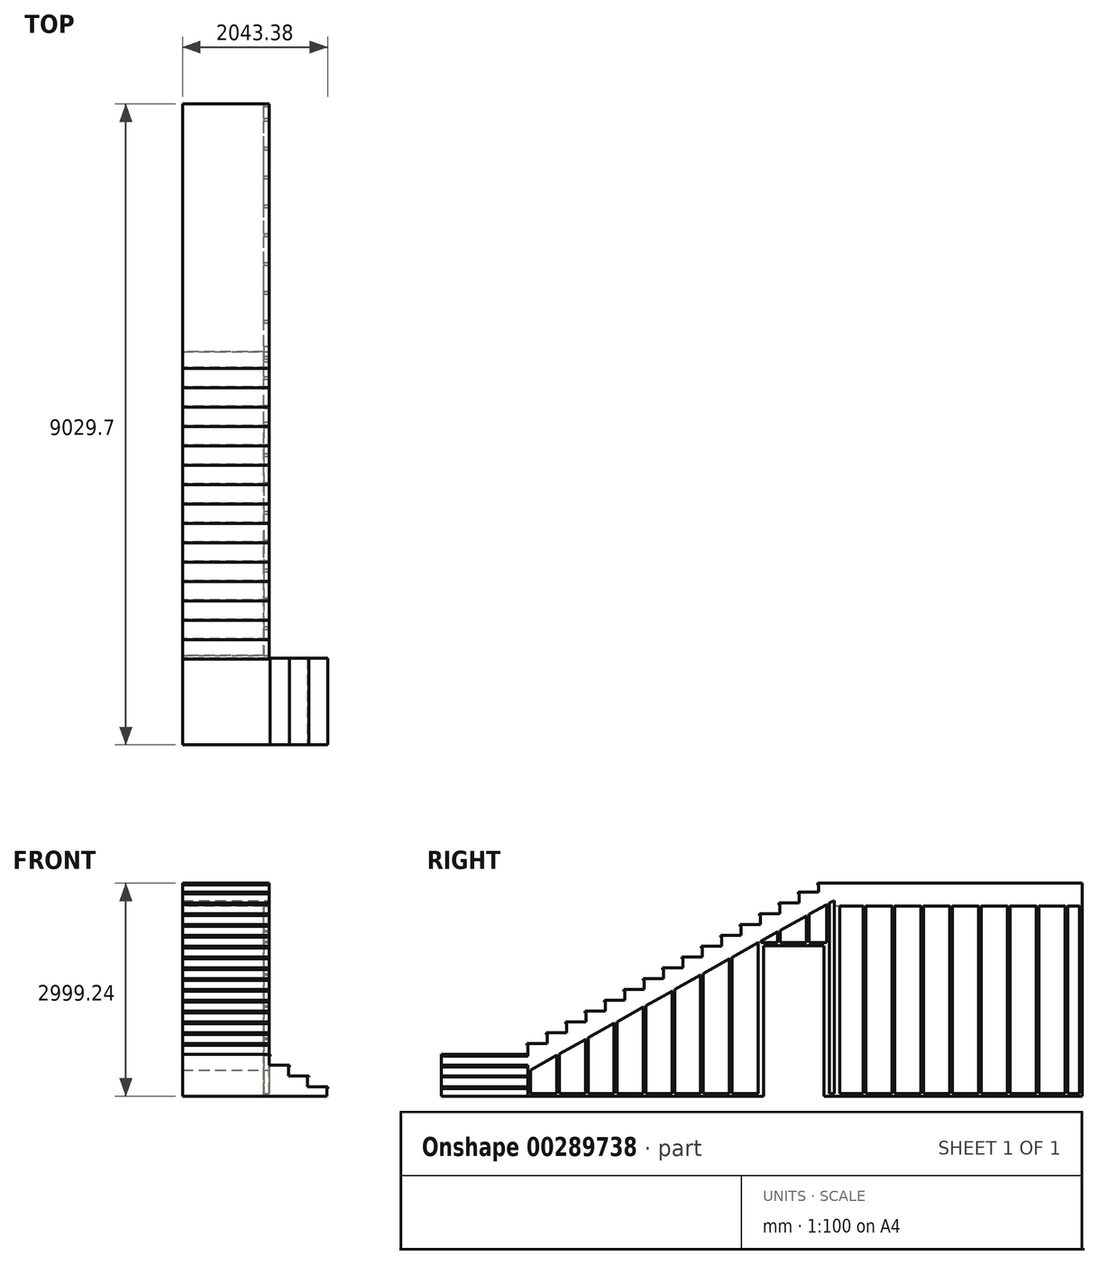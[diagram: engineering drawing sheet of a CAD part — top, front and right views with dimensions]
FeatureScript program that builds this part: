
annotation { "Feature Type Name" : "Feature", "Feature Type Description" : "" }
export const myFeature = defineFeature(function(context is Context, id is Id, definition is map)
    precondition{}
    {
        {
            var Q0;
            Q0=qCreatedBy(makeId("Right.planeOp"),FACE);
            var sketch = newSketch(context, id + "F0", { "sketchPlane" : qUnion([Q0])});
            skLineSegment(sketch, "E0.top", {"start": v(4540.25, 1499.62) * mm, "end": v(-4540.25, 1499.62) * mm});
            skLineSegment(sketch, "E0.left", {"start": v(4540.25, -1499.62) * mm, "end": v(4540.25, 1499.62) * mm});
            skLineSegment(sketch, "E0.right", {"start": v(-4540.25, -1499.62) * mm, "end": v(-4540.25, 1499.62) * mm});
            skPoint(sketch, "E0.middle", {"position": v(0, 0) * mm});
            skLineSegment(sketch, "E1", {"start": v(813.4, 1499.62) * mm, "end": v(813.4, 1478.97) * mm});
            skLineSegment(sketch, "E2", {"start": v(813.4, 1478.97) * mm, "end": v(826.1, 1478.97) * mm});
            skLineSegment(sketch, "E3", {"start": v(826.1, 1478.97) * mm, "end": v(826.1, 1371.6) * mm});
            skLineSegment(sketch, "E4", {"start": v(826.1, 1371.6) * mm, "end": v(540.36, 1371.6) * mm});
            skLineSegment(sketch, "E5", {"start": v(540.36, 1371.6) * mm, "end": v(540.36, 1350.87) * mm});
            skLineSegment(sketch, "E6", {"start": v(540.36, 1350.87) * mm, "end": v(553.16, 1350.87) * mm});
            skLineSegment(sketch, "E7", {"start": v(553.16, 1350.87) * mm, "end": v(553.16, 1219.2) * mm});
            skLineSegment(sketch, "E8", {"start": v(553.16, 1219.2) * mm, "end": v(267.26, 1219.2) * mm});
            skLineSegment(sketch, "E9", {"start": v(267.26, 1219.2) * mm, "end": v(267.26, 1198.47) * mm});
            skLineSegment(sketch, "E10", {"start": v(267.26, 1198.47) * mm, "end": v(280.06, 1198.47) * mm});
            skLineSegment(sketch, "E11", {"start": v(280.06, 1198.47) * mm, "end": v(280.06, 1066.8) * mm});
            skLineSegment(sketch, "E12", {"start": v(280.06, 1066.8) * mm, "end": v(-5.85, 1066.8) * mm});
            skLineSegment(sketch, "E13", {"start": v(-5.85, 1066.8) * mm, "end": v(-5.85, 1046.07) * mm});
            skLineSegment(sketch, "E14", {"start": v(-5.85, 1046.07) * mm, "end": v(6.96, 1046.07) * mm});
            skLineSegment(sketch, "E15", {"start": v(6.96, 1046.07) * mm, "end": v(6.96, 914.4) * mm});
            skLineSegment(sketch, "E16", {"start": v(6.96, 914.4) * mm, "end": v(-278.95, 914.4) * mm});
            skLineSegment(sketch, "E17", {"start": v(-278.95, 914.4) * mm, "end": v(-278.95, 893.67) * mm});
            skLineSegment(sketch, "E18", {"start": v(-278.95, 893.67) * mm, "end": v(-266.14, 893.67) * mm});
            skLineSegment(sketch, "E19", {"start": v(-266.14, 893.67) * mm, "end": v(-266.14, 762) * mm});
            skLineSegment(sketch, "E20", {"start": v(-266.14, 762) * mm, "end": v(-552.05, 762) * mm});
            skLineSegment(sketch, "E21", {"start": v(-552.05, 762) * mm, "end": v(-552.05, 741.27) * mm});
            skLineSegment(sketch, "E22", {"start": v(-552.05, 741.27) * mm, "end": v(-539.25, 741.27) * mm});
            skLineSegment(sketch, "E23", {"start": v(-539.25, 741.27) * mm, "end": v(-539.25, 609.6) * mm});
            skLineSegment(sketch, "E24", {"start": v(-539.25, 609.6) * mm, "end": v(-825.15, 609.6) * mm});
            skLineSegment(sketch, "E25", {"start": v(-825.15, 609.6) * mm, "end": v(-825.15, 588.87) * mm});
            skLineSegment(sketch, "E26", {"start": v(-825.15, 588.87) * mm, "end": v(-812.35, 588.87) * mm});
            skLineSegment(sketch, "E27", {"start": v(-812.35, 588.87) * mm, "end": v(-812.35, 457.2) * mm});
            skLineSegment(sketch, "E28", {"start": v(-812.35, 457.2) * mm, "end": v(-1098.25, 457.2) * mm});
            skLineSegment(sketch, "E29", {"start": v(-1098.25, 457.2) * mm, "end": v(-1098.25, 436.47) * mm});
            skLineSegment(sketch, "E30", {"start": v(-1098.25, 436.47) * mm, "end": v(-1085.45, 436.47) * mm});
            skLineSegment(sketch, "E31", {"start": v(-1085.45, 436.47) * mm, "end": v(-1085.45, 304.8) * mm});
            skLineSegment(sketch, "E32", {"start": v(-1085.45, 304.8) * mm, "end": v(-1371.35, 304.8) * mm});
            skLineSegment(sketch, "E33", {"start": v(-1371.35, 304.8) * mm, "end": v(-1371.35, 284.07) * mm});
            skLineSegment(sketch, "E34", {"start": v(-1371.35, 284.07) * mm, "end": v(-1358.55, 284.07) * mm});
            skLineSegment(sketch, "E35", {"start": v(-1358.55, 284.07) * mm, "end": v(-1358.55, 152.4) * mm});
            skLineSegment(sketch, "E36", {"start": v(-1358.55, 152.4) * mm, "end": v(-1644.45, 152.4) * mm});
            skLineSegment(sketch, "E37", {"start": v(-1644.45, 152.4) * mm, "end": v(-1644.45, 131.67) * mm});
            skLineSegment(sketch, "E38", {"start": v(-1644.45, 131.67) * mm, "end": v(-1631.65, 131.67) * mm});
            skLineSegment(sketch, "E39", {"start": v(-1631.65, 131.67) * mm, "end": v(-1631.65, 0) * mm});
            skLineSegment(sketch, "E40", {"start": v(-1631.65, 0) * mm, "end": v(-1917.55, 0) * mm});
            skLineSegment(sketch, "E41", {"start": v(-1917.55, 0) * mm, "end": v(-1917.55, -20.73) * mm});
            skLineSegment(sketch, "E42", {"start": v(-1917.55, -20.73) * mm, "end": v(-1904.75, -20.73) * mm});
            skLineSegment(sketch, "E43", {"start": v(-1904.75, -20.73) * mm, "end": v(-1904.75, -152.4) * mm});
            skLineSegment(sketch, "E44", {"start": v(-1904.75, -152.4) * mm, "end": v(-2190.65, -152.4) * mm});
            skLineSegment(sketch, "E45", {"start": v(-2190.65, -152.4) * mm, "end": v(-2190.65, -173.13) * mm});
            skLineSegment(sketch, "E46", {"start": v(-2190.65, -173.13) * mm, "end": v(-2177.85, -173.13) * mm});
            skLineSegment(sketch, "E47", {"start": v(-2177.85, -173.13) * mm, "end": v(-2177.85, -304.8) * mm});
            skLineSegment(sketch, "E48", {"start": v(-2177.85, -304.8) * mm, "end": v(-2463.75, -304.8) * mm});
            skLineSegment(sketch, "E49", {"start": v(-2463.75, -304.8) * mm, "end": v(-2463.75, -325.53) * mm});
            skLineSegment(sketch, "E50", {"start": v(-2463.75, -325.53) * mm, "end": v(-2450.95, -325.53) * mm});
            skLineSegment(sketch, "E51", {"start": v(-2450.95, -325.53) * mm, "end": v(-2450.95, -457.2) * mm});
            skLineSegment(sketch, "E52", {"start": v(-2450.95, -457.2) * mm, "end": v(-2736.85, -457.2) * mm});
            skLineSegment(sketch, "E53", {"start": v(-2736.85, -457.2) * mm, "end": v(-2736.85, -477.93) * mm});
            skLineSegment(sketch, "E54", {"start": v(-2736.85, -477.93) * mm, "end": v(-2724.05, -477.93) * mm});
            skLineSegment(sketch, "E55", {"start": v(-2724.05, -477.93) * mm, "end": v(-2724.05, -609.6) * mm});
            skLineSegment(sketch, "E56", {"start": v(-2724.05, -609.6) * mm, "end": v(-3009.95, -609.6) * mm});
            skLineSegment(sketch, "E57", {"start": v(-3009.95, -609.6) * mm, "end": v(-3009.95, -630.33) * mm});
            skLineSegment(sketch, "E58", {"start": v(-3009.95, -630.33) * mm, "end": v(-2997.15, -630.33) * mm});
            skLineSegment(sketch, "E59", {"start": v(-2997.15, -630.33) * mm, "end": v(-2997.15, -762) * mm});
            skLineSegment(sketch, "E60", {"start": v(-2997.15, -762) * mm, "end": v(-3283.05, -762) * mm});
            skLineSegment(sketch, "E61", {"start": v(-3283.05, -762) * mm, "end": v(-3283.05, -782.73) * mm});
            skLineSegment(sketch, "E62", {"start": v(-3283.05, -782.73) * mm, "end": v(-3270.25, -782.73) * mm});
            skLineSegment(sketch, "E63", {"start": v(-3270.25, -782.73) * mm, "end": v(-3270.25, -914.4) * mm});
            skLineSegment(sketch, "E64", {"start": v(-3270.25, -914.4) * mm, "end": v(-4489.45, -914.4) * mm});
            skLineSegment(sketch, "E65", {"start": v(-4489.45, -914.4) * mm, "end": v(-4489.45, -1499.62) * mm});
            skLineSegment(sketch, "E66", {"start": v(-4540.25, -1499.62) * mm, "end": v(4540.25, -1499.62) * mm});
            skSolve(sketch);
        }
        {
            var Q0;
            {var subQ3=sQuery(id+"F0.wireOp",EDGE,"E1");Q0=makeQuery(id+"F0.imprint","IMPRINT",FACE,{"disambiguationData":[TD([[makeQuery(id+"F0.imprint","IMPRINT",EDGE,{"derivedFrom":subQ3}),1.0]])]});}
            extrude(context, id + "F1", {"entities" : qUnion([Q0]), "depth" : 2438.4 * mm, "offsetDistance" : 30.48 * mm});
        }
        {
            var Q0;
            Q0=makeQuery(id+"F1.opExtrude","SWEPT_FACE",FACE,{"disambiguationData":[OSD([sQuery(id+"F0.wireOp",EDGE,"E66")])]});
            var sketch = newSketch(context, id + "F2", { "sketchPlane" : qUnion([Q0])});
            skLineSegment(sketch, "E67", {"start": v(1219.2, -4540.25) * mm, "end": v(1219.2, 3270.25) * mm});
            skLineSegment(sketch, "E68", {"start": v(1219.2, 3270.25) * mm, "end": v(2438.4, 3270.25) * mm});
            skSolve(sketch);
        }
        {
            var Q0;
            {var subQ0=sQuery(id+"F2.wireOp",EDGE,"E67");Q0=makeQuery(id+"F2.imprint","IMPRINT",FACE,{"disambiguationData":[TD([[makeQuery(id+"F2.imprint","IMPRINT",EDGE,{"derivedFrom":subQ0}),-1.0]])]});}
            extrude(context, id + "F3", {"entities" : qUnion([Q0]), "operationType" : NewBodyOperationType.REMOVE, "oppositeDirection" : true, "depth" : 6096 * mm, "offsetDistance" : 30.48 * mm});
        }
        {
            var Q0;
            {var subQ0=sQuery(id+"F0.wireOp",EDGE,"E60");var subQ1=sQuery(id+"F0.wireOp",EDGE,"E61");var subQ2=sQuery(id+"F0.wireOp",EDGE,"E62");Q0=makeQuery(id+"F3.boolean.opBoolean","SPLIT",FACE,{"disambiguationData":[TD([makeQuery(id+"F1.opExtrude","SWEPT_FACE",FACE,{"disambiguationData":[OSD([subQ0])]})])],"derivedFrom":makeQuery(id+"F1.opExtrude","CAP_FACE",FACE,{"disambiguationData":[OSD([sQuery(id+"F0.wireOp",EDGE,"E0.top"),sQuery(id+"F0.wireOp",EDGE,"E0.left"),sQuery(id+"F0.wireOp",EDGE,"E1"),sQuery(id+"F0.wireOp",EDGE,"E2"),sQuery(id+"F0.wireOp",EDGE,"E3"),sQuery(id+"F0.wireOp",EDGE,"E4"),sQuery(id+"F0.wireOp",EDGE,"E5"),sQuery(id+"F0.wireOp",EDGE,"E6"),sQuery(id+"F0.wireOp",EDGE,"E7"),sQuery(id+"F0.wireOp",EDGE,"E8"),sQuery(id+"F0.wireOp",EDGE,"E9"),sQuery(id+"F0.wireOp",EDGE,"E10"),sQuery(id+"F0.wireOp",EDGE,"E11"),sQuery(id+"F0.wireOp",EDGE,"E12"),sQuery(id+"F0.wireOp",EDGE,"E13"),sQuery(id+"F0.wireOp",EDGE,"E14"),sQuery(id+"F0.wireOp",EDGE,"E15"),sQuery(id+"F0.wireOp",EDGE,"E16"),sQuery(id+"F0.wireOp",EDGE,"E17"),sQuery(id+"F0.wireOp",EDGE,"E18"),sQuery(id+"F0.wireOp",EDGE,"E19"),sQuery(id+"F0.wireOp",EDGE,"E20"),sQuery(id+"F0.wireOp",EDGE,"E21"),sQuery(id+"F0.wireOp",EDGE,"E22"),sQuery(id+"F0.wireOp",EDGE,"E23"),sQuery(id+"F0.wireOp",EDGE,"E24"),sQuery(id+"F0.wireOp",EDGE,"E25"),sQuery(id+"F0.wireOp",EDGE,"E26"),sQuery(id+"F0.wireOp",EDGE,"E27"),sQuery(id+"F0.wireOp",EDGE,"E28"),sQuery(id+"F0.wireOp",EDGE,"E29"),sQuery(id+"F0.wireOp",EDGE,"E30"),sQuery(id+"F0.wireOp",EDGE,"E31"),sQuery(id+"F0.wireOp",EDGE,"E32"),sQuery(id+"F0.wireOp",EDGE,"E33"),sQuery(id+"F0.wireOp",EDGE,"E34"),sQuery(id+"F0.wireOp",EDGE,"E35"),sQuery(id+"F0.wireOp",EDGE,"E36"),sQuery(id+"F0.wireOp",EDGE,"E37"),sQuery(id+"F0.wireOp",EDGE,"E38"),sQuery(id+"F0.wireOp",EDGE,"E39"),sQuery(id+"F0.wireOp",EDGE,"E40"),sQuery(id+"F0.wireOp",EDGE,"E41"),sQuery(id+"F0.wireOp",EDGE,"E42"),sQuery(id+"F0.wireOp",EDGE,"E43"),sQuery(id+"F0.wireOp",EDGE,"E44"),sQuery(id+"F0.wireOp",EDGE,"E45"),sQuery(id+"F0.wireOp",EDGE,"E46"),sQuery(id+"F0.wireOp",EDGE,"E47"),sQuery(id+"F0.wireOp",EDGE,"E48"),sQuery(id+"F0.wireOp",EDGE,"E49"),sQuery(id+"F0.wireOp",EDGE,"E50"),sQuery(id+"F0.wireOp",EDGE,"E51"),sQuery(id+"F0.wireOp",EDGE,"E52"),sQuery(id+"F0.wireOp",EDGE,"E53"),sQuery(id+"F0.wireOp",EDGE,"E54"),sQuery(id+"F0.wireOp",EDGE,"E55"),sQuery(id+"F0.wireOp",EDGE,"E56"),sQuery(id+"F0.wireOp",EDGE,"E57"),sQuery(id+"F0.wireOp",EDGE,"E58"),sQuery(id+"F0.wireOp",EDGE,"E59"),subQ0,subQ1,subQ2,sQuery(id+"F0.wireOp",EDGE,"E63"),sQuery(id+"F0.wireOp",EDGE,"E64"),sQuery(id+"F0.wireOp",EDGE,"E65"),sQuery(id+"F0.wireOp",EDGE,"E66")])],"isStart":false})});}
            extrude(context, id + "F4", {"entities" : qUnion([Q0]), "operationType" : NewBodyOperationType.REMOVE, "oppositeDirection" : true, "depth" : 1219.2 * mm, "offsetDistance" : 30.48 * mm});
        }
        {
            var Q0;
            Q0=makeQuery(id+"F1.opExtrude","SWEPT_FACE",FACE,{"disambiguationData":[OSD([sQuery(id+"F0.wireOp",EDGE,"E65")])]});
            var sketch = newSketch(context, id + "F5", { "sketchPlane" : qUnion([Q0])});
            skLineSegment(sketch, "E69", {"start": v(1232, -914.4) * mm, "end": v(1232, -935.13) * mm});
            skLineSegment(sketch, "E70", {"start": v(1232, -935.13) * mm, "end": v(1219.2, -935.13) * mm});
            skLineSegment(sketch, "E71", {"start": v(1219.2, -935.13) * mm, "end": v(1219.2, -1066.8) * mm});
            skLineSegment(sketch, "E72", {"start": v(1219.2, -1066.8) * mm, "end": v(1505.1, -1066.8) * mm});
            skLineSegment(sketch, "E73", {"start": v(1505.1, -1066.8) * mm, "end": v(1505.1, -1087.53) * mm});
            skLineSegment(sketch, "E74", {"start": v(1505.1, -1087.53) * mm, "end": v(1492.3, -1087.53) * mm});
            skLineSegment(sketch, "E75", {"start": v(1492.3, -1087.53) * mm, "end": v(1492.3, -1219.2) * mm});
            skLineSegment(sketch, "E76", {"start": v(1492.3, -1219.2) * mm, "end": v(1778.2, -1219.2) * mm});
            skLineSegment(sketch, "E77", {"start": v(1778.2, -1219.2) * mm, "end": v(1778.2, -1232) * mm});
            skLineSegment(sketch, "E78", {"start": v(1778.2, -1232) * mm, "end": v(1757.48, -1232) * mm});
            skLineSegment(sketch, "E79", {"start": v(1757.48, -1232) * mm, "end": v(1757.48, -1371.6) * mm});
            skLineSegment(sketch, "E80", {"start": v(1757.48, -1371.6) * mm, "end": v(2043.38, -1371.6) * mm});
            skLineSegment(sketch, "E81", {"start": v(2043.38, -1371.6) * mm, "end": v(2043.38, -1392.33) * mm});
            skLineSegment(sketch, "E82", {"start": v(2043.38, -1392.33) * mm, "end": v(2030.58, -1392.33) * mm});
            skLineSegment(sketch, "E83", {"start": v(2030.58, -1392.33) * mm, "end": v(2030.58, -1499.62) * mm});
            skSolve(sketch);
        }
        {
            var Q0;
            Q0 = qSketchRegion(id + "F5", true);
            var Q1;
            {var subQ0=sQuery(id+"F5.wireOp",EDGE,"E69");Q1=makeQuery(id+"F5.imprint","IMPRINT",FACE,{"disambiguationData":[TD([[makeQuery(id+"F5.imprint","IMPRINT",EDGE,{"derivedFrom":subQ0}),1.0]])]});}
            extrude(context, id + "F6", {"entities" : qUnion([Q0, Q1]), "operationType" : NewBodyOperationType.REMOVE, "oppositeDirection" : true, "depth" : 12192 * mm, "offsetDistance" : 30.48 * mm});
        }
        {
            var Q0;
            Q0=makeQuery(id+"F6.boolean.opBoolean","MERGE",FACE,{"derivedFrom":[makeQuery(id+"F4.boolean.opBoolean","MERGE",FACE,{"derivedFrom":[makeQuery(id+"F3.boolean.opBoolean","COPY",FACE,{"derivedFrom":makeQuery(id+"F3.opExtrude","SWEPT_FACE",FACE,{"disambiguationData":[OSD([sQuery(id+"F2.wireOp",EDGE,"E67")])]})})],"fromTools":[makeQuery(id+"F4.opExtrude","CAP_FACE",FACE,{"disambiguationData":[OSD([sQuery(id+"F0.wireOp",EDGE,"E0.top"),sQuery(id+"F0.wireOp",EDGE,"E0.left"),sQuery(id+"F0.wireOp",EDGE,"E1"),sQuery(id+"F0.wireOp",EDGE,"E2"),sQuery(id+"F0.wireOp",EDGE,"E3"),sQuery(id+"F0.wireOp",EDGE,"E4"),sQuery(id+"F0.wireOp",EDGE,"E5"),sQuery(id+"F0.wireOp",EDGE,"E6"),sQuery(id+"F0.wireOp",EDGE,"E7"),sQuery(id+"F0.wireOp",EDGE,"E8"),sQuery(id+"F0.wireOp",EDGE,"E9"),sQuery(id+"F0.wireOp",EDGE,"E10"),sQuery(id+"F0.wireOp",EDGE,"E11"),sQuery(id+"F0.wireOp",EDGE,"E12"),sQuery(id+"F0.wireOp",EDGE,"E13"),sQuery(id+"F0.wireOp",EDGE,"E14"),sQuery(id+"F0.wireOp",EDGE,"E15"),sQuery(id+"F0.wireOp",EDGE,"E16"),sQuery(id+"F0.wireOp",EDGE,"E17"),sQuery(id+"F0.wireOp",EDGE,"E18"),sQuery(id+"F0.wireOp",EDGE,"E19"),sQuery(id+"F0.wireOp",EDGE,"E20"),sQuery(id+"F0.wireOp",EDGE,"E21"),sQuery(id+"F0.wireOp",EDGE,"E22"),sQuery(id+"F0.wireOp",EDGE,"E23"),sQuery(id+"F0.wireOp",EDGE,"E24"),sQuery(id+"F0.wireOp",EDGE,"E25"),sQuery(id+"F0.wireOp",EDGE,"E26"),sQuery(id+"F0.wireOp",EDGE,"E27"),sQuery(id+"F0.wireOp",EDGE,"E28"),sQuery(id+"F0.wireOp",EDGE,"E29"),sQuery(id+"F0.wireOp",EDGE,"E30"),sQuery(id+"F0.wireOp",EDGE,"E31"),sQuery(id+"F0.wireOp",EDGE,"E32"),sQuery(id+"F0.wireOp",EDGE,"E33"),sQuery(id+"F0.wireOp",EDGE,"E34"),sQuery(id+"F0.wireOp",EDGE,"E35"),sQuery(id+"F0.wireOp",EDGE,"E36"),sQuery(id+"F0.wireOp",EDGE,"E37"),sQuery(id+"F0.wireOp",EDGE,"E38"),sQuery(id+"F0.wireOp",EDGE,"E39"),sQuery(id+"F0.wireOp",EDGE,"E40"),sQuery(id+"F0.wireOp",EDGE,"E41"),sQuery(id+"F0.wireOp",EDGE,"E42"),sQuery(id+"F0.wireOp",EDGE,"E43"),sQuery(id+"F0.wireOp",EDGE,"E44"),sQuery(id+"F0.wireOp",EDGE,"E45"),sQuery(id+"F0.wireOp",EDGE,"E46"),sQuery(id+"F0.wireOp",EDGE,"E47"),sQuery(id+"F0.wireOp",EDGE,"E48"),sQuery(id+"F0.wireOp",EDGE,"E49"),sQuery(id+"F0.wireOp",EDGE,"E50"),sQuery(id+"F0.wireOp",EDGE,"E51"),sQuery(id+"F0.wireOp",EDGE,"E52"),sQuery(id+"F0.wireOp",EDGE,"E53"),sQuery(id+"F0.wireOp",EDGE,"E54"),sQuery(id+"F0.wireOp",EDGE,"E55"),sQuery(id+"F0.wireOp",EDGE,"E56"),sQuery(id+"F0.wireOp",EDGE,"E57"),sQuery(id+"F0.wireOp",EDGE,"E58"),sQuery(id+"F0.wireOp",EDGE,"E59"),sQuery(id+"F0.wireOp",EDGE,"E60"),sQuery(id+"F0.wireOp",EDGE,"E61"),sQuery(id+"F0.wireOp",EDGE,"E62"),sQuery(id+"F0.wireOp",EDGE,"E63"),sQuery(id+"F0.wireOp",EDGE,"E64"),sQuery(id+"F0.wireOp",EDGE,"E65"),sQuery(id+"F0.wireOp",EDGE,"E66")])],"isStart":false})]})],"fromTools":[makeQuery(id+"F6.opExtrude","SWEPT_FACE",FACE,{"disambiguationData":[OSD([sQuery(id+"F5.wireOp",EDGE,"E71")])]})]});
            var sketch = newSketch(context, id + "F7", { "sketchPlane" : qUnion([Q0])});
            skLineSegment(sketch, "E84", {"start": v(1406.1, 1499.62) * mm, "end": v(-3270.25, -1109.96) * mm});
            skLineSegment(sketch, "E85", {"start": v(-2997.15, -762) * mm, "end": v(-2724.05, -609.6) * mm});
            skLineSegment(sketch, "E86", {"start": v(1049.26, 1300.49) * mm, "end": v(1049.26, 1499.62) * mm});
            skLineSegment(sketch, "E87.bottom", {"start": v(1087.36, 1213.87) * mm, "end": v(4502.15, 1213.87) * mm});
            skLineSegment(sketch, "E87.top", {"start": v(1087.36, -1461.52) * mm, "end": v(4502.15, -1461.52) * mm});
            skLineSegment(sketch, "E87.left", {"start": v(1087.36, 1213.87) * mm, "end": v(1087.36, -1461.52) * mm});
            skLineSegment(sketch, "E87.right", {"start": v(4502.15, 1213.87) * mm, "end": v(4502.15, -1461.52) * mm});
            skLineSegment(sketch, "E88", {"start": v(1049.26, 1300.49) * mm, "end": v(1049.26, -1461.52) * mm});
            skLineSegment(sketch, "E89", {"start": v(1049.26, -1461.52) * mm, "end": v(-3232.15, -1461.52) * mm});
            skLineSegment(sketch, "E90", {"start": v(-3232.15, -1461.52) * mm, "end": v(-3232.15, -1132.33) * mm});
            skLineSegment(sketch, "E91", {"start": v(-3232.15, -1132.33) * mm, "end": v(1049.26, 1256.85) * mm});
            skLineSegment(sketch, "E92", {"start": v(-2825.85, -905.6) * mm, "end": v(-2825.85, -1461.52) * mm});
            skLineSegment(sketch, "E93", {"start": v(-2863.95, -926.86) * mm, "end": v(-2863.95, -1461.52) * mm});
            skLineSegment(sketch, "E94", {"start": v(-2457.66, -700.13) * mm, "end": v(-2457.66, -1461.52) * mm});
            skLineSegment(sketch, "E95", {"start": v(-2419.56, -678.87) * mm, "end": v(-2419.56, -1461.52) * mm});
            skLineSegment(sketch, "E96", {"start": v(-2051.36, -473.4) * mm, "end": v(-2051.36, -1461.52) * mm});
            skLineSegment(sketch, "E97", {"start": v(-2013.26, -452.14) * mm, "end": v(-2013.26, -1461.52) * mm});
            skLineSegment(sketch, "E98", {"start": v(-1645.06, -246.67) * mm, "end": v(-1645.06, -1461.52) * mm});
            skLineSegment(sketch, "E99", {"start": v(-1606.96, -225.41) * mm, "end": v(-1606.96, -1461.52) * mm});
            skLineSegment(sketch, "E100", {"start": v(-1238.76, -19.94) * mm, "end": v(-1238.76, -1461.52) * mm});
            skLineSegment(sketch, "E101", {"start": v(-1200.66, -1461.52) * mm, "end": v(-1200.66, 1.32) * mm});
            skLineSegment(sketch, "E102", {"start": v(-832.46, 206.79) * mm, "end": v(-832.46, -1461.52) * mm});
            skLineSegment(sketch, "E103", {"start": v(-794.36, 228.05) * mm, "end": v(-794.36, -1461.52) * mm});
            skLineSegment(sketch, "E104", {"start": v(-426.16, 433.51) * mm, "end": v(-426.16, -1461.52) * mm});
            skLineSegment(sketch, "E105", {"start": v(-388.06, 454.78) * mm, "end": v(-388.06, -1461.52) * mm});
            skLineSegment(sketch, "E106", {"start": v(-19.87, 660.24) * mm, "end": v(-19.87, -1461.52) * mm});
            skLineSegment(sketch, "E107", {"start": v(18.23, 681.5) * mm, "end": v(18.23, -1461.52) * mm});
            skLineSegment(sketch, "E108", {"start": v(1087.36, 1175.77) * mm, "end": v(4502.15, 1175.77) * mm});
            skLineSegment(sketch, "E109.bottom", {"start": v(1455.56, 1175.77) * mm, "end": v(1493.66, 1175.77) * mm});
            skLineSegment(sketch, "E109.top", {"start": v(1455.56, -1461.52) * mm, "end": v(1493.66, -1461.52) * mm});
            skLineSegment(sketch, "E109.left", {"start": v(1455.56, 1175.77) * mm, "end": v(1455.56, -1461.52) * mm});
            skLineSegment(sketch, "E109.right", {"start": v(1493.66, 1175.77) * mm, "end": v(1493.66, -1461.52) * mm});
            skLineSegment(sketch, "E110.bottom", {"start": v(1861.86, 1175.77) * mm, "end": v(1899.96, 1175.77) * mm});
            skLineSegment(sketch, "E110.top", {"start": v(1861.86, -1461.52) * mm, "end": v(1899.96, -1461.52) * mm});
            skLineSegment(sketch, "E110.left", {"start": v(1861.86, 1175.77) * mm, "end": v(1861.86, -1461.52) * mm});
            skLineSegment(sketch, "E110.right", {"start": v(1899.96, 1175.77) * mm, "end": v(1899.96, -1461.52) * mm});
            skLineSegment(sketch, "E111.bottom", {"start": v(56.33, -1499.62) * mm, "end": v(907.23, -1499.62) * mm});
            skLineSegment(sketch, "E111.top", {"start": v(56.33, 621.28) * mm, "end": v(907.23, 621.28) * mm});
            skLineSegment(sketch, "E111.left", {"start": v(56.33, -1499.62) * mm, "end": v(56.33, 621.28) * mm});
            skLineSegment(sketch, "E111.right", {"start": v(907.23, -1499.62) * mm, "end": v(907.23, 621.28) * mm});
            skLineSegment(sketch, "E112.bottom", {"start": v(907.23, 621.28) * mm, "end": v(945.33, 621.28) * mm});
            skLineSegment(sketch, "E112.top", {"start": v(907.23, -1461.52) * mm, "end": v(945.33, -1461.52) * mm});
            skLineSegment(sketch, "E112.left", {"start": v(907.23, 621.28) * mm, "end": v(907.23, -1461.52) * mm});
            skLineSegment(sketch, "E112.right", {"start": v(945.33, 621.28) * mm, "end": v(945.33, -1461.52) * mm});
            skLineSegment(sketch, "E113.bottom", {"start": v(945.33, -1461.52) * mm, "end": v(983.43, -1461.52) * mm});
            skLineSegment(sketch, "E113.top", {"start": v(945.33, 1220.12) * mm, "end": v(983.43, 1220.12) * mm});
            skLineSegment(sketch, "E113.left", {"start": v(945.33, -1461.52) * mm, "end": v(945.33, 1220.12) * mm});
            skLineSegment(sketch, "E113.right", {"start": v(983.43, -1461.52) * mm, "end": v(983.43, 1220.12) * mm});
            skLineSegment(sketch, "E114", {"start": v(18.23, 660.24) * mm, "end": v(945.33, 660.24) * mm});
            skLineSegment(sketch, "E115.bottom", {"start": v(253.13, 660.24) * mm, "end": v(291.23, 660.24) * mm});
            skLineSegment(sketch, "E115.top", {"start": v(253.13, 833.85) * mm, "end": v(291.23, 833.85) * mm});
            skLineSegment(sketch, "E115.left", {"start": v(253.13, 660.24) * mm, "end": v(253.13, 833.85) * mm});
            skLineSegment(sketch, "E115.right", {"start": v(291.23, 660.24) * mm, "end": v(291.23, 833.85) * mm});
            skLineSegment(sketch, "E116.bottom", {"start": v(659.43, 660.24) * mm, "end": v(697.53, 660.24) * mm});
            skLineSegment(sketch, "E116.top", {"start": v(659.43, 1060.58) * mm, "end": v(697.53, 1060.58) * mm});
            skLineSegment(sketch, "E116.left", {"start": v(659.43, 660.24) * mm, "end": v(659.43, 1060.58) * mm});
            skLineSegment(sketch, "E116.right", {"start": v(697.53, 660.24) * mm, "end": v(697.53, 1060.58) * mm});
            skLineSegment(sketch, "E117.bottom", {"start": v(2268.16, 1175.77) * mm, "end": v(2306.26, 1175.77) * mm});
            skLineSegment(sketch, "E117.top", {"start": v(2268.16, -1461.52) * mm, "end": v(2306.26, -1461.52) * mm});
            skLineSegment(sketch, "E117.left", {"start": v(2268.16, 1175.77) * mm, "end": v(2268.16, -1461.52) * mm});
            skLineSegment(sketch, "E117.right", {"start": v(2306.26, 1175.77) * mm, "end": v(2306.26, -1461.52) * mm});
            skLineSegment(sketch, "E118.bottom", {"start": v(2674.45, 1175.77) * mm, "end": v(2712.55, 1175.77) * mm});
            skLineSegment(sketch, "E118.top", {"start": v(2674.45, -1461.52) * mm, "end": v(2712.55, -1461.52) * mm});
            skLineSegment(sketch, "E118.left", {"start": v(2674.45, 1175.77) * mm, "end": v(2674.45, -1461.52) * mm});
            skLineSegment(sketch, "E118.right", {"start": v(2712.55, 1175.77) * mm, "end": v(2712.55, -1461.52) * mm});
            skLineSegment(sketch, "E119.bottom", {"start": v(3080.75, 1175.77) * mm, "end": v(3118.85, 1175.77) * mm});
            skLineSegment(sketch, "E119.top", {"start": v(3080.75, -1461.52) * mm, "end": v(3118.85, -1461.52) * mm});
            skLineSegment(sketch, "E119.left", {"start": v(3080.75, 1175.77) * mm, "end": v(3080.75, -1461.52) * mm});
            skLineSegment(sketch, "E119.right", {"start": v(3118.85, 1175.77) * mm, "end": v(3118.85, -1461.52) * mm});
            skLineSegment(sketch, "E120.bottom", {"start": v(3487.05, 1175.77) * mm, "end": v(3525.15, 1175.77) * mm});
            skLineSegment(sketch, "E120.top", {"start": v(3487.05, -1461.52) * mm, "end": v(3525.15, -1461.52) * mm});
            skLineSegment(sketch, "E120.left", {"start": v(3487.05, 1175.77) * mm, "end": v(3487.05, -1461.52) * mm});
            skLineSegment(sketch, "E120.right", {"start": v(3525.15, 1175.77) * mm, "end": v(3525.15, -1461.52) * mm});
            skLineSegment(sketch, "E121.bottom", {"start": v(3893.35, 1175.77) * mm, "end": v(3931.45, 1175.77) * mm});
            skLineSegment(sketch, "E121.top", {"start": v(3893.35, -1461.52) * mm, "end": v(3931.45, -1461.52) * mm});
            skLineSegment(sketch, "E121.left", {"start": v(3893.35, 1175.77) * mm, "end": v(3893.35, -1461.52) * mm});
            skLineSegment(sketch, "E121.right", {"start": v(3931.45, 1175.77) * mm, "end": v(3931.45, -1461.52) * mm});
            skLineSegment(sketch, "E122.bottom", {"start": v(4299.65, 1175.77) * mm, "end": v(4337.75, 1175.77) * mm});
            skLineSegment(sketch, "E122.top", {"start": v(4299.65, -1461.52) * mm, "end": v(4337.75, -1461.52) * mm});
            skLineSegment(sketch, "E122.left", {"start": v(4299.65, 1175.77) * mm, "end": v(4299.65, -1461.52) * mm});
            skLineSegment(sketch, "E122.right", {"start": v(4337.75, 1175.77) * mm, "end": v(4337.75, -1461.52) * mm});
            skLineSegment(sketch, "E123.bottom", {"start": v(1087.36, 1175.77) * mm, "end": v(1125.46, 1175.77) * mm});
            skLineSegment(sketch, "E123.top", {"start": v(1087.36, -1461.52) * mm, "end": v(1125.46, -1461.52) * mm});
            skLineSegment(sketch, "E123.left", {"start": v(1087.36, 1175.77) * mm, "end": v(1087.36, -1461.52) * mm});
            skLineSegment(sketch, "E123.right", {"start": v(1125.46, 1175.77) * mm, "end": v(1125.46, -1461.52) * mm});
            skSolve(sketch);
        }
        {
            var Q0;
            {var subQ0=sQuery(id+"F7.wireOp",EDGE,"E90");Q0=makeQuery(id+"F7.imprint","IMPRINT",FACE,{"disambiguationData":[TD([[makeQuery(id+"F7.imprint","IMPRINT",EDGE,{"derivedFrom":subQ0}),-1.0]])]});}
            var Q1;
            {var subQ2=sQuery(id+"F7.wireOp",EDGE,"E92");Q1=makeQuery(id+"F7.imprint","IMPRINT",FACE,{"disambiguationData":[TD([[makeQuery(id+"F7.imprint","IMPRINT",EDGE,{"derivedFrom":subQ2}),1.0]])]});}
            var Q2;
            {var subQ0=sQuery(id+"F7.wireOp",EDGE,"E95");Q2=makeQuery(id+"F7.imprint","IMPRINT",FACE,{"disambiguationData":[TD([[makeQuery(id+"F7.imprint","IMPRINT",EDGE,{"derivedFrom":subQ0}),1.0]])]});}
            var Q3;
            {var subQ0=sQuery(id+"F7.wireOp",EDGE,"E97");Q3=makeQuery(id+"F7.imprint","IMPRINT",FACE,{"disambiguationData":[TD([[makeQuery(id+"F7.imprint","IMPRINT",EDGE,{"derivedFrom":subQ0}),1.0]])]});}
            var Q4;
            {var subQ0=sQuery(id+"F7.wireOp",EDGE,"E99");Q4=makeQuery(id+"F7.imprint","IMPRINT",FACE,{"disambiguationData":[TD([[makeQuery(id+"F7.imprint","IMPRINT",EDGE,{"derivedFrom":subQ0}),1.0]])]});}
            var Q5;
            {var subQ0=sQuery(id+"F7.wireOp",EDGE,"E101");Q5=makeQuery(id+"F7.imprint","IMPRINT",FACE,{"disambiguationData":[TD([[makeQuery(id+"F7.imprint","IMPRINT",EDGE,{"derivedFrom":subQ0}),-1.0]])]});}
            var Q6;
            {var subQ0=sQuery(id+"F7.wireOp",EDGE,"E103");Q6=makeQuery(id+"F7.imprint","IMPRINT",FACE,{"disambiguationData":[TD([[makeQuery(id+"F7.imprint","IMPRINT",EDGE,{"derivedFrom":subQ0}),1.0]])]});}
            var Q7;
            {var subQ0=sQuery(id+"F7.wireOp",EDGE,"E105");Q7=makeQuery(id+"F7.imprint","IMPRINT",FACE,{"disambiguationData":[TD([[makeQuery(id+"F7.imprint","IMPRINT",EDGE,{"derivedFrom":subQ0}),1.0]])]});}
            var Q8;
            {var subQ5=sQuery(id+"F7.wireOp",EDGE,"E111.top");Q8=makeQuery(id+"F7.imprint","IMPRINT",FACE,{"disambiguationData":[TD([[makeQuery(id+"F7.imprint","IMPRINT",EDGE,{"derivedFrom":subQ5}),-1.0]])]});}
            var Q9;
            {var subQ0=sQuery(id+"F7.wireOp",EDGE,"E107");var subQ1=sQuery(id+"F7.wireOp",EDGE,"E91");var subQ2=makeQuery(id+"F7.imprint","INTERSECT",VERTEX,{"derivedFrom":[subQ1,subQ0]});Q9=makeQuery(id+"F7.imprint","IMPRINT",FACE,{"disambiguationData":[TD([[makeQuery(id+"F7.imprint","IMPRINT",EDGE,{"disambiguationData":[TD([[subQ2,-1.0]])],"derivedFrom":subQ1}),-1.0]])]});}
            var Q10;
            {var subQ0=sQuery(id+"F7.wireOp",EDGE,"E115.right");Q10=makeQuery(id+"F7.imprint","IMPRINT",FACE,{"disambiguationData":[TD([[makeQuery(id+"F7.imprint","IMPRINT",EDGE,{"derivedFrom":subQ0}),-1.0]])]});}
            var Q11;
            {var subQ0=sQuery(id+"F7.wireOp",EDGE,"E116.right");Q11=makeQuery(id+"F7.imprint","IMPRINT",FACE,{"disambiguationData":[TD([[makeQuery(id+"F7.imprint","IMPRINT",EDGE,{"derivedFrom":subQ0}),-1.0]])]});}
            var Q12;
            {var subQ5=sQuery(id+"F7.wireOp",EDGE,"E113.right");Q12=makeQuery(id+"F7.imprint","IMPRINT",FACE,{"disambiguationData":[TD([[makeQuery(id+"F7.imprint","IMPRINT",EDGE,{"derivedFrom":subQ5}),-1.0]])]});}
            var Q13;
            {var subQ2=sQuery(id+"F7.wireOp",EDGE,"E109.left");Q13=makeQuery(id+"F7.imprint","IMPRINT",FACE,{"disambiguationData":[TD([[makeQuery(id+"F7.imprint","IMPRINT",EDGE,{"derivedFrom":subQ2}),-1.0]])]});}
            var Q14;
            {var subQ0=sQuery(id+"F7.wireOp",EDGE,"E109.right");Q14=makeQuery(id+"F7.imprint","IMPRINT",FACE,{"disambiguationData":[TD([[makeQuery(id+"F7.imprint","IMPRINT",EDGE,{"derivedFrom":subQ0}),1.0]])]});}
            var Q15;
            {var subQ0=sQuery(id+"F7.wireOp",EDGE,"E110.right");Q15=makeQuery(id+"F7.imprint","IMPRINT",FACE,{"disambiguationData":[TD([[makeQuery(id+"F7.imprint","IMPRINT",EDGE,{"derivedFrom":subQ0}),1.0]])]});}
            var Q16;
            {var subQ0=sQuery(id+"F7.wireOp",EDGE,"E117.right");Q16=makeQuery(id+"F7.imprint","IMPRINT",FACE,{"disambiguationData":[TD([[makeQuery(id+"F7.imprint","IMPRINT",EDGE,{"derivedFrom":subQ0}),1.0]])]});}
            var Q17;
            {var subQ0=sQuery(id+"F7.wireOp",EDGE,"E118.right");Q17=makeQuery(id+"F7.imprint","IMPRINT",FACE,{"disambiguationData":[TD([[makeQuery(id+"F7.imprint","IMPRINT",EDGE,{"derivedFrom":subQ0}),1.0]])]});}
            var Q18;
            {var subQ0=sQuery(id+"F7.wireOp",EDGE,"E119.right");Q18=makeQuery(id+"F7.imprint","IMPRINT",FACE,{"disambiguationData":[TD([[makeQuery(id+"F7.imprint","IMPRINT",EDGE,{"derivedFrom":subQ0}),1.0]])]});}
            var Q19;
            {var subQ0=sQuery(id+"F7.wireOp",EDGE,"E120.right");Q19=makeQuery(id+"F7.imprint","IMPRINT",FACE,{"disambiguationData":[TD([[makeQuery(id+"F7.imprint","IMPRINT",EDGE,{"derivedFrom":subQ0}),1.0]])]});}
            var Q20;
            {var subQ0=sQuery(id+"F7.wireOp",EDGE,"E121.right");Q20=makeQuery(id+"F7.imprint","IMPRINT",FACE,{"disambiguationData":[TD([[makeQuery(id+"F7.imprint","IMPRINT",EDGE,{"derivedFrom":subQ0}),1.0]])]});}
            var Q21;
            {var subQ0=sQuery(id+"F7.wireOp",EDGE,"E122.right");Q21=makeQuery(id+"F7.imprint","IMPRINT",FACE,{"disambiguationData":[TD([[makeQuery(id+"F7.imprint","IMPRINT",EDGE,{"derivedFrom":subQ0}),1.0]])]});}
            var Q22;
            {var subQ5=sQuery(id+"F7.wireOp",EDGE,"E111.bottom");Q22=makeQuery(id+"F7.imprint","IMPRINT",FACE,{"disambiguationData":[TD([[makeQuery(id+"F7.imprint","IMPRINT",EDGE,{"derivedFrom":subQ5}),-1.0]])]});}
            extrude(context, id + "F8", {"entities" : qUnion([Q0, Q1, Q2, Q3, Q4, Q5, Q6, Q7, Q8, Q9, Q10, Q11, Q12, Q13, Q14, Q15, Q16, Q17, Q18, Q19, Q20, Q21, Q22]), "operationType" : NewBodyOperationType.REMOVE, "oppositeDirection" : true, "depth" : 1524 * mm, "offsetDistance" : 30.48 * mm});
        }
        {
            var Q0;
            Q0=makeQuery(id+"F1.opExtrude","CAP_FACE",FACE,{"disambiguationData":[OSD([sQuery(id+"F0.wireOp",EDGE,"E0.top"),sQuery(id+"F0.wireOp",EDGE,"E0.left"),sQuery(id+"F0.wireOp",EDGE,"E1"),sQuery(id+"F0.wireOp",EDGE,"E2"),sQuery(id+"F0.wireOp",EDGE,"E3"),sQuery(id+"F0.wireOp",EDGE,"E4"),sQuery(id+"F0.wireOp",EDGE,"E5"),sQuery(id+"F0.wireOp",EDGE,"E6"),sQuery(id+"F0.wireOp",EDGE,"E7"),sQuery(id+"F0.wireOp",EDGE,"E8"),sQuery(id+"F0.wireOp",EDGE,"E9"),sQuery(id+"F0.wireOp",EDGE,"E10"),sQuery(id+"F0.wireOp",EDGE,"E11"),sQuery(id+"F0.wireOp",EDGE,"E12"),sQuery(id+"F0.wireOp",EDGE,"E13"),sQuery(id+"F0.wireOp",EDGE,"E14"),sQuery(id+"F0.wireOp",EDGE,"E15"),sQuery(id+"F0.wireOp",EDGE,"E16"),sQuery(id+"F0.wireOp",EDGE,"E17"),sQuery(id+"F0.wireOp",EDGE,"E18"),sQuery(id+"F0.wireOp",EDGE,"E19"),sQuery(id+"F0.wireOp",EDGE,"E20"),sQuery(id+"F0.wireOp",EDGE,"E21"),sQuery(id+"F0.wireOp",EDGE,"E22"),sQuery(id+"F0.wireOp",EDGE,"E23"),sQuery(id+"F0.wireOp",EDGE,"E24"),sQuery(id+"F0.wireOp",EDGE,"E25"),sQuery(id+"F0.wireOp",EDGE,"E26"),sQuery(id+"F0.wireOp",EDGE,"E27"),sQuery(id+"F0.wireOp",EDGE,"E28"),sQuery(id+"F0.wireOp",EDGE,"E29"),sQuery(id+"F0.wireOp",EDGE,"E30"),sQuery(id+"F0.wireOp",EDGE,"E31"),sQuery(id+"F0.wireOp",EDGE,"E32"),sQuery(id+"F0.wireOp",EDGE,"E33"),sQuery(id+"F0.wireOp",EDGE,"E34"),sQuery(id+"F0.wireOp",EDGE,"E35"),sQuery(id+"F0.wireOp",EDGE,"E36"),sQuery(id+"F0.wireOp",EDGE,"E37"),sQuery(id+"F0.wireOp",EDGE,"E38"),sQuery(id+"F0.wireOp",EDGE,"E39"),sQuery(id+"F0.wireOp",EDGE,"E40"),sQuery(id+"F0.wireOp",EDGE,"E41"),sQuery(id+"F0.wireOp",EDGE,"E42"),sQuery(id+"F0.wireOp",EDGE,"E43"),sQuery(id+"F0.wireOp",EDGE,"E44"),sQuery(id+"F0.wireOp",EDGE,"E45"),sQuery(id+"F0.wireOp",EDGE,"E46"),sQuery(id+"F0.wireOp",EDGE,"E47"),sQuery(id+"F0.wireOp",EDGE,"E48"),sQuery(id+"F0.wireOp",EDGE,"E49"),sQuery(id+"F0.wireOp",EDGE,"E50"),sQuery(id+"F0.wireOp",EDGE,"E51"),sQuery(id+"F0.wireOp",EDGE,"E52"),sQuery(id+"F0.wireOp",EDGE,"E53"),sQuery(id+"F0.wireOp",EDGE,"E54"),sQuery(id+"F0.wireOp",EDGE,"E55"),sQuery(id+"F0.wireOp",EDGE,"E56"),sQuery(id+"F0.wireOp",EDGE,"E57"),sQuery(id+"F0.wireOp",EDGE,"E58"),sQuery(id+"F0.wireOp",EDGE,"E59"),sQuery(id+"F0.wireOp",EDGE,"E60"),sQuery(id+"F0.wireOp",EDGE,"E61"),sQuery(id+"F0.wireOp",EDGE,"E62"),sQuery(id+"F0.wireOp",EDGE,"E63"),sQuery(id+"F0.wireOp",EDGE,"E64"),sQuery(id+"F0.wireOp",EDGE,"E65"),sQuery(id+"F0.wireOp",EDGE,"E66")])],"isStart":true});
            var sketch = newSketch(context, id + "F9", { "sketchPlane" : qUnion([Q0])});
            skLineSegment(sketch, "E124", {"start": v(-4540.25, 1175.77) * mm, "end": v(-1049.26, 1175.77) * mm});
            skLineSegment(sketch, "E125", {"start": v(-1049.26, 1256.85) * mm, "end": v(3232.15, -1132.33) * mm});
            skLineSegment(sketch, "E126", {"start": v(3232.15, -1132.33) * mm, "end": v(3232.15, -1499.62) * mm});
            skLineSegment(sketch, "E127", {"start": v(3232.15, -1499.62) * mm, "end": v(-4540.25, -1499.62) * mm});
            skLineSegment(sketch, "E128", {"start": v(-4540.25, -1499.62) * mm, "end": v(-4540.25, 1175.77) * mm});
            skSolve(sketch);
        }
        {
            var Q0;
            {var subQ54=sQuery(id+"F9.wireOp",EDGE,"E127");Q0=makeQuery(id+"F9.imprint","IMPRINT",FACE,{"disambiguationData":[TD([[makeQuery(id+"F9.imprint","IMPRINT",EDGE,{"derivedFrom":subQ54}),-1.0]])]});}
            extrude(context, id + "F10", {"entities" : qUnion([Q0]), "operationType" : NewBodyOperationType.REMOVE, "oppositeDirection" : true, "depth" : 1143 * mm, "offsetDistance" : 30.48 * mm});
        }
    });
